# Revit family: RFL4
name_source: partatom
category: Lighting Fixtures
revit_build: Autodesk Revit 2014 (Build: 20130308_1515(x64)
units: mm (PartAtom-declared; Revit-internal decimal feet)

## types (1)
- RFL4
    Apparent Load = 120 VA
    Assembly Code = D5020200
    Certifications = UL 1598 Standard for Luminaires,IP66 certified.
    Color Filter = 16777215
    Connector Description = Lighting Connector
    Default Elevation = 48 "
    Description = Compact LED flood with a variety of NEMA distribution for lighting applications such as safety/security, accent, flag pole, columns, or signs. The Ratio flood series was designed in cohesion with the site/area products to provide a sleek yet timeless product family to be used throughout a site. Ratio features a dense optical array which provides reduced pixelation and increased visual comfort without compromising performance
    Dimming Lamp Color Temperature Shift = <None>
    Features = Lumen range from 2,000 to 4,000 lm
• Color Temperature 3000K, 4000K, 5000K at
70 and 80 CRI
• Yoke and Threaded Knuckle mounting options.
• 6 beam distributions and beam angles
including: Narrow 17°x17°, Medium 28°x27°,
Medium Flood 62°x61°, Wide 79°x64°,
Horizontal 54°x22°, and Vertical 22°x54°.
• IP66 sealed optical and driver chamber
    Housing Material = Paint - Hubbell - Carbon Black
    LED = RFL
    LED_Finish = Glass - Hubbell - White
    Lamp = LED
    Length = 26.38 "
    Load Classification = Lighting
    Manufacturer = Hubbell Lighting
    Model = RFL4
    Photometric Note = For more ies file please find the above Photometric Web Link
    Photometric Web File = RFL4-176L-120-4K7-M.IES
    Photometric Web Link = https://www.hubbell.com
    Power Factor = 1
    Product Doucmentation Link = https://hubbellcdn.com
    Product Page URL = https://www.hubbell.com
    Reflector Finish = Hubbell - White Glass
    Screw = Metal-Hubbell-Gray
    Tilt Angle = 0.00°
    URL = https://www.hubbell.com
    Voltage = 120 V
    Warranty = 5 years Warranty
    Wattage Comments = 120W
    Watts = 120 W
    Width = 11.63 "
    Width 1 = 5 "

## geometry (parser evidence)
native form markers: Sweep x5
no freeform markers — native parametric forms only
